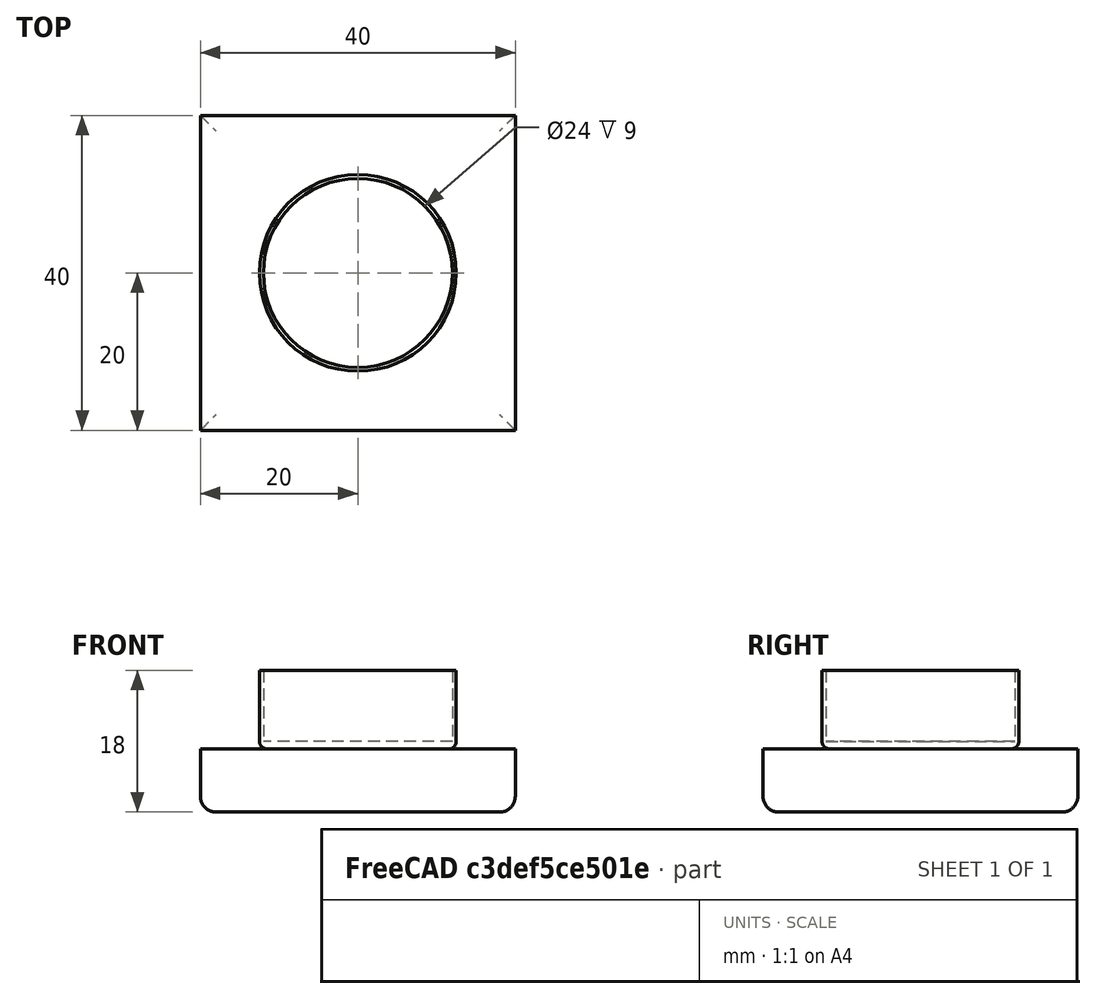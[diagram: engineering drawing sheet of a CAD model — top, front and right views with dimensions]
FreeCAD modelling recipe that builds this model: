
FCSTD DOCUMENT  (FreeCAD 0.20R29603 (Git))
Label: HomeCookingRobot
License: All rights reserved
LicenseURL: http://en.wikipedia.org/wiki/All_rights_reserved
objects: PartDesign::Fillet×2, PartDesign::Body×2, PartDesign::AdditiveBox×1, PartDesign::AdditiveCylinder×1, PartDesign::Hole×1
note: 12 computed .brp shape members not serialized (recipe doc carries the construction recipe); baked Part::Feature solids carry a one-line shape summary decoded from their .brp

FEATURE [PartDesign::AdditiveBox] Box
  AttacherType = Attacher::AttachEngine3D
  AttachmentOffset = pos=(-20,-20,0) rot=(0,0,1;0rad)
  Height = 8
  Length = 40
  MapMode = 5
  Placement = pos=(-20,-20,0) rot=(0,0,1;0rad)
  Refine = true
  Support = -> [XY_Plane]
  Width = 40
  expr: .AttachmentOffset.Base.x = -Length * 0.5
  expr: .AttachmentOffset.Base.y = -Width * 0.5
  expr: Width = Length
FEATURE [PartDesign::Fillet] Fillet
  Base = -> Box [Edge9,Edge8,Edge11,Edge4]
  BaseFeature = -> Box
  Placement = pos=(-20,-20,0) rot=(0,0,1;0rad)
  Radius = 2
  Refine = true
  SupportTransform = false
  UseAllEdges = false
FEATURE [PartDesign::Body] Body  label="ElectricStove"
  Group = -> [Box,Fillet]
  Origin = -> Origin
  Tip = -> Fillet
FEATURE [PartDesign::AdditiveCylinder] Cylinder
  Angle = 360
  AttacherType = Attacher::AttachEngine3D
  FirstAngle = 0
  Height = 10
  MapMode = 45
  Placement = pos=(0,0,8) rot=(0,0,1;0rad)
  Radius = 12.5
  Refine = true
  SecondAngle = 0
  Support = -> [Fillet]
FEATURE [PartDesign::Hole] Hole
  BaseFeature = -> Cylinder
  CustomThreadClearance = 0
  Depth = 9
  DepthType = 0
  Diameter = 24
  DrillForDepth = false
  DrillPoint = 0
  DrillPointAngle = 118
  HoleCutCountersinkAngle = 90
  HoleCutCustomValues = false
  HoleCutDepth = 0
  HoleCutDiameter = 6.1
  HoleCutType = 0
  ModelThread = false
  Placement = pos=(0,0,8) rot=(0,0,1;0rad)
  Profile = -> Cylinder [Edge3]
  Refine = true
  Tapered = false
  TaperedAngle = 90
  ThreadClass = 0
  ThreadDepth = 9
  ThreadDepthType = 0
  ThreadDirection = 0
  ThreadFit = 0
  ThreadSize = 0
  ThreadType = 0
  Threaded = false
  UseCustomThreadClearance = false
FEATURE [PartDesign::Fillet] Fillet001
  Base = -> Hole [Edge2]
  BaseFeature = -> Hole
  Placement = pos=(0,0,8) rot=(0,0,1;0rad)
  Radius = 1
  Refine = true
  SupportTransform = false
  UseAllEdges = false
FEATURE [PartDesign::Body] Body001  label="CookingVessel"
  Group = -> [Cylinder,Hole,Fillet001]
  Origin = -> Origin001
  Tip = -> Fillet001
